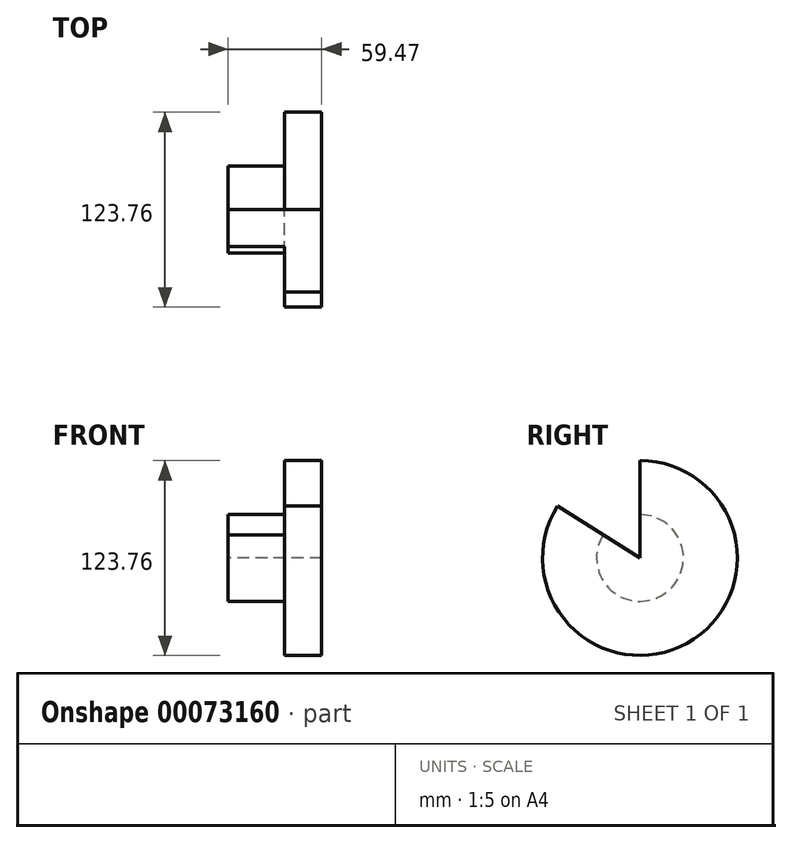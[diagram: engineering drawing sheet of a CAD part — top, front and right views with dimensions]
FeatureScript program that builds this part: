
annotation { "Feature Type Name" : "Feature", "Feature Type Description" : "" }
export const myFeature = defineFeature(function(context is Context, id is Id, definition is map)
    precondition{}
    {
        {
            var Q0;
            Q0=qCreatedBy(makeId("Front.planeOp"),FACE);
            var sketch = newSketch(context, id + "F0", { "sketchPlane" : qUnion([Q0])});
            skLineSegment(sketch, "E0", {"start": v(0, 0) * mm, "end": v(-59.47, 0) * mm});
            skLineSegment(sketch, "E1", {"start": v(-59.47, 0) * mm, "end": v(-59.47, 27.54) * mm});
            skLineSegment(sketch, "E2", {"start": v(-59.47, 27.54) * mm, "end": v(-23.53, 27.54) * mm});
            skLineSegment(sketch, "E3", {"start": v(-23.53, 27.54) * mm, "end": v(-23.53, 61.88) * mm});
            skLineSegment(sketch, "E4", {"start": v(-23.53, 61.88) * mm, "end": v(0, 61.88) * mm});
            skLineSegment(sketch, "E5", {"start": v(0, 61.88) * mm, "end": v(0, 0) * mm});
            skSolve(sketch);
        }
        {
            var Q0;
            Q0=makeQuery(id+"F0.imprint","IMPRINT",FACE,{"disambiguationData":[TD([[makeQuery(id+"F0.imprint","IMPRINT",EDGE,{"derivedFrom":sQuery(id+"F0.wireOp",EDGE,"E0")}),-1.0]])]});
            var Q1;
            Q1=sQuery(id+"F0.wireOp",EDGE,"E0");
            revolve(context, id + "F1", {"entities" : qUnion([Q0]), "axis" : qUnion([Q1]), "revolveType" : RevolveType.ONE_DIRECTION, "angle" : 302.2 * degree});
        }
    });
